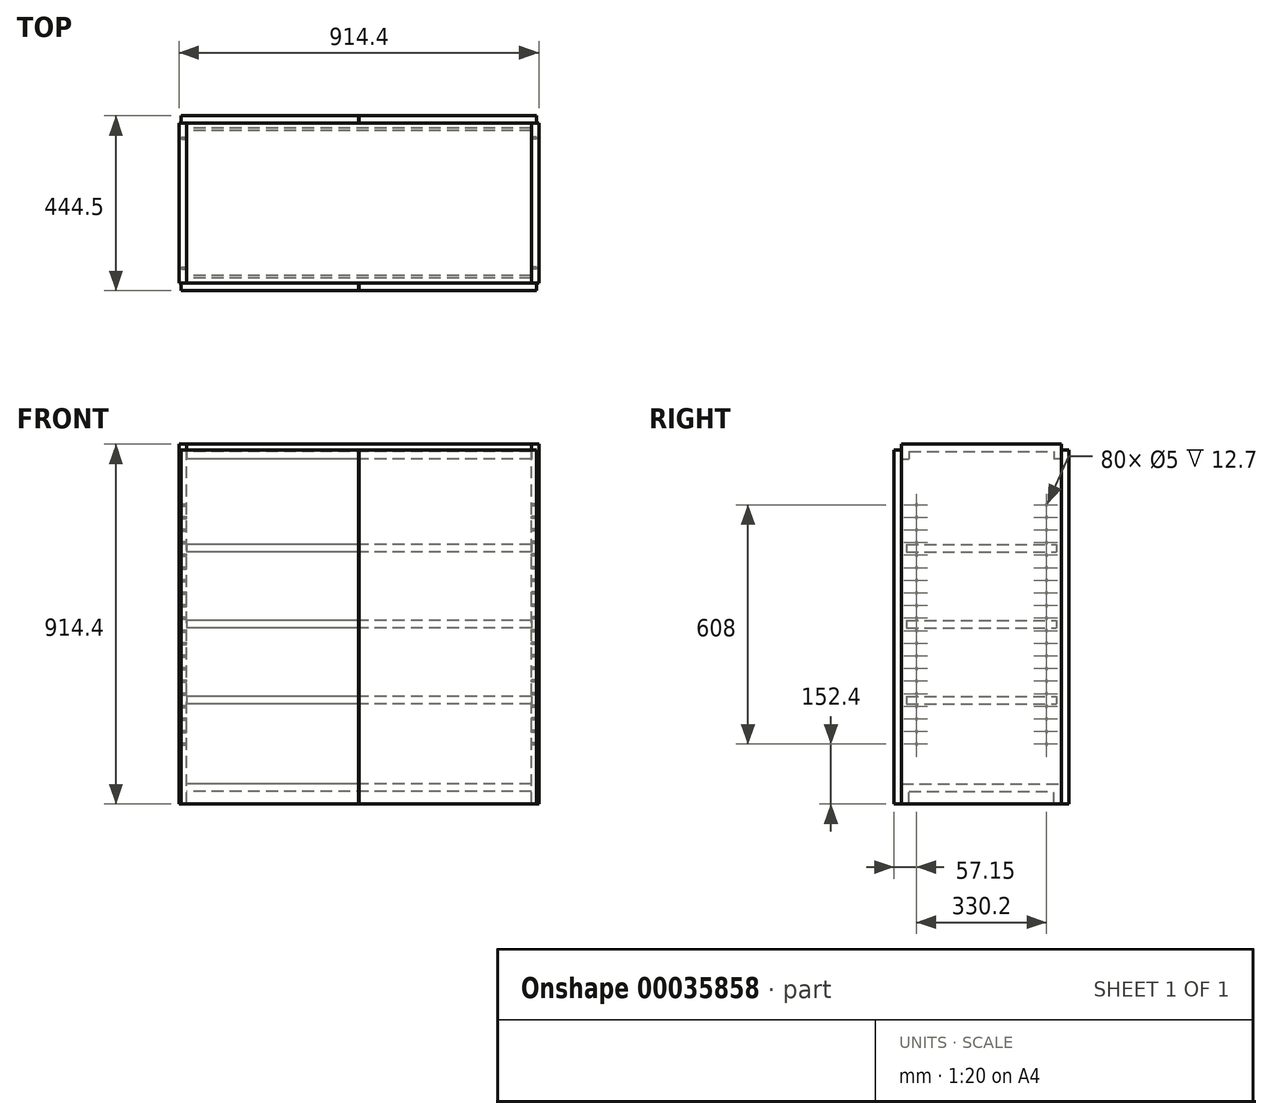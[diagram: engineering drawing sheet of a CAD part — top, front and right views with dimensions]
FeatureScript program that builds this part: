
annotation { "Feature Type Name" : "Feature", "Feature Type Description" : "" }
export const myFeature = defineFeature(function(context is Context, id is Id, definition is map)
    precondition{}
    {
        {
            var Q0;
            Q0=qCreatedBy(makeId("Right.planeOp"),FACE);
            var sketch = newSketch(context, id + "F0", { "sketchPlane" : qUnion([Q0])});
            skLineSegment(sketch, "E0.bottom", {"start": v(0, 0) * mm, "end": v(406.4, 0) * mm});
            skLineSegment(sketch, "E0.top", {"start": v(0, 914.4) * mm, "end": v(406.4, 914.4) * mm});
            skLineSegment(sketch, "E0.left", {"start": v(0, 0) * mm, "end": v(0, 914.4) * mm});
            skLineSegment(sketch, "E0.right", {"start": v(406.4, 0) * mm, "end": v(406.4, 914.4) * mm});
            skSolve(sketch);
        }
        {
            var Q0;
            Q0 = qSketchRegion(id + "F0", true);
            extrude(context, id + "F1", {"entities" : qUnion([Q0]), "depth" : 19.05 * mm});
        }
        {
            var Q0;
            Q0=makeQuery(id+"F1.opExtrude","CAP_FACE",FACE,{"disambiguationData":[OSD([sQuery(id+"F0.wireOp",EDGE,"E0.bottom"),sQuery(id+"F0.wireOp",EDGE,"E0.top"),sQuery(id+"F0.wireOp",EDGE,"E0.left"),sQuery(id+"F0.wireOp",EDGE,"E0.right")])],"isStart":false});
            var sketch = newSketch(context, id + "F2", { "sketchPlane" : qUnion([Q0])});
            skCircle(sketch, "E1", {"center": v(38.1, 152.4) * mm, "radius": 2.5 * mm});
            skCircle(sketch, "E2.0.1.0", {"center": v(38.1, 184.4) * mm, "radius": 2.5 * mm});
            skCircle(sketch, "E2.0.2.0", {"center": v(38.1, 216.4) * mm, "radius": 2.5 * mm});
            skCircle(sketch, "E2.0.3.0", {"center": v(38.1, 248.4) * mm, "radius": 2.5 * mm});
            skCircle(sketch, "E2.0.4.0", {"center": v(38.1, 280.4) * mm, "radius": 2.5 * mm});
            skCircle(sketch, "E2.0.5.0", {"center": v(38.1, 312.4) * mm, "radius": 2.5 * mm});
            skCircle(sketch, "E2.0.6.0", {"center": v(38.1, 344.4) * mm, "radius": 2.5 * mm});
            skCircle(sketch, "E2.0.7.0", {"center": v(38.1, 376.4) * mm, "radius": 2.5 * mm});
            skCircle(sketch, "E2.0.8.0", {"center": v(38.1, 408.4) * mm, "radius": 2.5 * mm});
            skCircle(sketch, "E2.0.9.0", {"center": v(38.1, 440.4) * mm, "radius": 2.5 * mm});
            skCircle(sketch, "E2.0.10.0", {"center": v(38.1, 472.4) * mm, "radius": 2.5 * mm});
            skCircle(sketch, "E2.0.11.0", {"center": v(38.1, 504.4) * mm, "radius": 2.5 * mm});
            skCircle(sketch, "E2.0.12.0", {"center": v(38.1, 536.4) * mm, "radius": 2.5 * mm});
            skCircle(sketch, "E2.0.13.0", {"center": v(38.1, 568.4) * mm, "radius": 2.5 * mm});
            skCircle(sketch, "E2.0.14.0", {"center": v(38.1, 600.4) * mm, "radius": 2.5 * mm});
            skCircle(sketch, "E2.0.15.0", {"center": v(38.1, 632.4) * mm, "radius": 2.5 * mm});
            skCircle(sketch, "E2.0.16.0", {"center": v(38.1, 664.4) * mm, "radius": 2.5 * mm});
            skCircle(sketch, "E2.0.17.0", {"center": v(38.1, 696.4) * mm, "radius": 2.5 * mm});
            skCircle(sketch, "E2.0.18.0", {"center": v(38.1, 728.4) * mm, "radius": 2.5 * mm});
            skCircle(sketch, "E2.0.19.0", {"center": v(38.1, 760.4) * mm, "radius": 2.5 * mm});
            skCircle(sketch, "E2.1.0.0", {"center": v(368.3, 152.4) * mm, "radius": 2.5 * mm});
            skCircle(sketch, "E2.1.1.0", {"center": v(368.3, 184.4) * mm, "radius": 2.5 * mm});
            skCircle(sketch, "E2.1.2.0", {"center": v(368.3, 216.4) * mm, "radius": 2.5 * mm});
            skCircle(sketch, "E2.1.3.0", {"center": v(368.3, 248.4) * mm, "radius": 2.5 * mm});
            skCircle(sketch, "E2.1.4.0", {"center": v(368.3, 280.4) * mm, "radius": 2.5 * mm});
            skCircle(sketch, "E2.1.5.0", {"center": v(368.3, 312.4) * mm, "radius": 2.5 * mm});
            skCircle(sketch, "E2.1.6.0", {"center": v(368.3, 344.4) * mm, "radius": 2.5 * mm});
            skCircle(sketch, "E2.1.7.0", {"center": v(368.3, 376.4) * mm, "radius": 2.5 * mm});
            skCircle(sketch, "E2.1.8.0", {"center": v(368.3, 408.4) * mm, "radius": 2.5 * mm});
            skCircle(sketch, "E2.1.9.0", {"center": v(368.3, 440.4) * mm, "radius": 2.5 * mm});
            skCircle(sketch, "E2.1.10.0", {"center": v(368.3, 472.4) * mm, "radius": 2.5 * mm});
            skCircle(sketch, "E2.1.11.0", {"center": v(368.3, 504.4) * mm, "radius": 2.5 * mm});
            skCircle(sketch, "E2.1.12.0", {"center": v(368.3, 536.4) * mm, "radius": 2.5 * mm});
            skCircle(sketch, "E2.1.13.0", {"center": v(368.3, 568.4) * mm, "radius": 2.5 * mm});
            skCircle(sketch, "E2.1.14.0", {"center": v(368.3, 600.4) * mm, "radius": 2.5 * mm});
            skCircle(sketch, "E2.1.15.0", {"center": v(368.3, 632.4) * mm, "radius": 2.5 * mm});
            skCircle(sketch, "E2.1.16.0", {"center": v(368.3, 664.4) * mm, "radius": 2.5 * mm});
            skCircle(sketch, "E2.1.17.0", {"center": v(368.3, 696.4) * mm, "radius": 2.5 * mm});
            skCircle(sketch, "E2.1.18.0", {"center": v(368.3, 728.4) * mm, "radius": 2.5 * mm});
            skCircle(sketch, "E2.1.19.0", {"center": v(368.3, 760.4) * mm, "radius": 2.5 * mm});
            skLineSegment(sketch, "E2.direction1", {"start": v(38.1, 152.4) * mm, "end": v(368.3, 152.4) * mm, "construction": true});
            skLineSegment(sketch, "E2.direction2", {"start": v(38.1, 152.4) * mm, "end": v(38.1, 184.4) * mm, "construction": true});
            skSolve(sketch);
        }
        {
            var Q0;
            Q0 = qSketchRegion(id + "F2", true);
            extrude(context, id + "F3", {"entities" : qUnion([Q0]), "operationType" : NewBodyOperationType.REMOVE, "oppositeDirection" : true, "depth" : 12.7 * mm});
        }
        {
            var Q0;
            Q0=makeQuery(id+"F1.opExtrude","CAP_FACE",FACE,{"disambiguationData":[OSD([sQuery(id+"F0.wireOp",EDGE,"E0.bottom"),sQuery(id+"F0.wireOp",EDGE,"E0.top"),sQuery(id+"F0.wireOp",EDGE,"E0.left"),sQuery(id+"F0.wireOp",EDGE,"E0.right")])],"isStart":false});
            var sketch = newSketch(context, id + "F4", { "sketchPlane" : qUnion([Q0])});
            skLineSegment(sketch, "E3.bottom", {"start": v(0, 914.4) * mm, "end": v(19.05, 914.4) * mm});
            skLineSegment(sketch, "E3.top", {"start": v(0, 876.3) * mm, "end": v(19.05, 876.3) * mm});
            skLineSegment(sketch, "E3.left", {"start": v(0, 914.4) * mm, "end": v(0, 876.3) * mm});
            skLineSegment(sketch, "E3.right", {"start": v(19.05, 914.4) * mm, "end": v(19.05, 876.3) * mm});
            skLineSegment(sketch, "E4.bottom", {"start": v(406.4, 914.4) * mm, "end": v(387.35, 914.4) * mm});
            skLineSegment(sketch, "E4.top", {"start": v(406.4, 876.3) * mm, "end": v(387.35, 876.3) * mm});
            skLineSegment(sketch, "E4.left", {"start": v(406.4, 914.4) * mm, "end": v(406.4, 876.3) * mm});
            skLineSegment(sketch, "E4.right", {"start": v(387.35, 914.4) * mm, "end": v(387.35, 876.3) * mm});
            skLineSegment(sketch, "E5.bottom", {"start": v(19.05, 914.4) * mm, "end": v(387.35, 914.4) * mm});
            skLineSegment(sketch, "E5.top", {"start": v(19.05, 895.35) * mm, "end": v(387.35, 895.35) * mm});
            skLineSegment(sketch, "E5.left", {"start": v(19.05, 914.4) * mm, "end": v(19.05, 895.35) * mm});
            skLineSegment(sketch, "E5.right", {"start": v(387.35, 914.4) * mm, "end": v(387.35, 895.35) * mm});
            skLineSegment(sketch, "E6.bottom", {"start": v(0, 0) * mm, "end": v(19.05, 0) * mm});
            skLineSegment(sketch, "E6.top", {"start": v(0, 50.8) * mm, "end": v(19.05, 50.8) * mm});
            skLineSegment(sketch, "E6.left", {"start": v(0, 0) * mm, "end": v(0, 50.8) * mm});
            skLineSegment(sketch, "E6.right", {"start": v(19.05, 0) * mm, "end": v(19.05, 50.8) * mm});
            skLineSegment(sketch, "E7.bottom", {"start": v(406.4, 0) * mm, "end": v(387.35, 0) * mm});
            skLineSegment(sketch, "E7.top", {"start": v(406.4, 50.8) * mm, "end": v(387.35, 50.8) * mm});
            skLineSegment(sketch, "E7.left", {"start": v(406.4, 0) * mm, "end": v(406.4, 50.8) * mm});
            skLineSegment(sketch, "E7.right", {"start": v(387.35, 0) * mm, "end": v(387.35, 50.8) * mm});
            skLineSegment(sketch, "E8.bottom", {"start": v(19.05, 50.8) * mm, "end": v(387.35, 50.8) * mm});
            skLineSegment(sketch, "E8.top", {"start": v(19.05, 32.58) * mm, "end": v(387.35, 32.58) * mm});
            skLineSegment(sketch, "E8.left", {"start": v(19.05, 50.8) * mm, "end": v(19.05, 32.58) * mm});
            skLineSegment(sketch, "E8.right", {"start": v(387.35, 50.8) * mm, "end": v(387.35, 32.58) * mm});
            skLineSegment(sketch, "E9.bottom", {"start": v(12.7, 273.28) * mm, "end": v(393.7, 273.28) * mm});
            skLineSegment(sketch, "E9.top", {"start": v(12.7, 254.23) * mm, "end": v(393.7, 254.23) * mm});
            skLineSegment(sketch, "E9.left", {"start": v(12.7, 273.28) * mm, "end": v(12.7, 254.23) * mm});
            skLineSegment(sketch, "E9.right", {"start": v(393.7, 273.28) * mm, "end": v(393.7, 254.23) * mm});
            skLineSegment(sketch, "E10.0.1.0", {"start": v(12.7, 447.27) * mm, "end": v(393.7, 447.27) * mm});
            skLineSegment(sketch, "E10.0.1.1", {"start": v(12.7, 466.32) * mm, "end": v(12.7, 447.27) * mm});
            skLineSegment(sketch, "E10.0.1.2", {"start": v(12.7, 466.32) * mm, "end": v(393.7, 466.32) * mm});
            skLineSegment(sketch, "E10.0.1.3", {"start": v(393.7, 466.32) * mm, "end": v(393.7, 447.27) * mm});
            skLineSegment(sketch, "E10.0.2.0", {"start": v(12.7, 640.3) * mm, "end": v(393.7, 640.3) * mm});
            skLineSegment(sketch, "E10.0.2.1", {"start": v(12.7, 659.36) * mm, "end": v(12.7, 640.3) * mm});
            skLineSegment(sketch, "E10.0.2.2", {"start": v(12.7, 659.36) * mm, "end": v(393.7, 659.36) * mm});
            skLineSegment(sketch, "E10.0.2.3", {"start": v(393.7, 659.36) * mm, "end": v(393.7, 640.3) * mm});
            skLineSegment(sketch, "E10.direction1", {"start": v(12.7, 254.23) * mm, "end": v(38.1, 254.23) * mm, "construction": true});
            skLineSegment(sketch, "E10.direction2", {"start": v(12.7, 254.23) * mm, "end": v(12.7, 447.27) * mm, "construction": true});
            skSolve(sketch);
        }
        {
            var Q0;
            Q0=qCreatedBy(makeId("Right.planeOp"),FACE);
            cPlane(context, id + "F5", {"entities" : qUnion([Q0]), "cplaneType" : CPlaneType.OFFSET, "offset" : 457.2 * mm, "width" : 152.4 * mm, "height" : 152.4 * mm});
        }
        {
            var Q0;
            {var subQ0=sQuery(id+"F4.wireOp",EDGE,"E8.bottom");var subQ10=sQuery(id+"F4.wireOp",EDGE,"E7.bottom");var subQ12=sQuery(id+"F4.wireOp",EDGE,"E6.bottom");var subQ13=sQuery(id+"F4.wireOp",EDGE,"E5.bottom");var subQ15=sQuery(id+"F4.wireOp",EDGE,"E3.bottom");var subQ20=sQuery(id+"F4.wireOp",EDGE,"E4.bottom");Q0=qUnion([makeQuery(id+"F4.imprint","IMPRINT",FACE,{"disambiguationData":[TD([[makeQuery(id+"F4.imprint","IMPRINT",EDGE,{"derivedFrom":sQuery(id+"F4.wireOp",EDGE,"E9.bottom")}),-1.0]])]}),makeQuery(id+"F4.imprint","IMPRINT",FACE,{"disambiguationData":[TD([[makeQuery(id+"F4.imprint","IMPRINT",EDGE,{"derivedFrom":sQuery(id+"F4.wireOp",EDGE,"E10.0.1.0")}),1.0]])]}),makeQuery(id+"F4.imprint","IMPRINT",FACE,{"disambiguationData":[TD([[makeQuery(id+"F4.imprint","IMPRINT",EDGE,{"derivedFrom":sQuery(id+"F4.wireOp",EDGE,"E10.0.2.0")}),1.0]])]}),makeQuery(id+"F4.imprint","IMPRINT",FACE,{"disambiguationData":[TD([[makeQuery(id+"F4.imprint","IMPRINT",EDGE,{"derivedFrom":subQ15}),-1.0]])]}),makeQuery(id+"F4.imprint","IMPRINT",FACE,{"disambiguationData":[TD([[makeQuery(id+"F4.imprint","IMPRINT",EDGE,{"derivedFrom":subQ20}),-1.0]])]}),makeQuery(id+"F4.imprint","IMPRINT",FACE,{"disambiguationData":[TD([[makeQuery(id+"F4.imprint","IMPRINT",EDGE,{"derivedFrom":subQ13}),-1.0]])]}),makeQuery(id+"F4.imprint","IMPRINT",FACE,{"disambiguationData":[TD([[makeQuery(id+"F4.imprint","IMPRINT",EDGE,{"derivedFrom":subQ12}),1.0]])]}),makeQuery(id+"F4.imprint","IMPRINT",FACE,{"disambiguationData":[TD([[makeQuery(id+"F4.imprint","IMPRINT",EDGE,{"derivedFrom":subQ10}),1.0]])]}),makeQuery(id+"F4.imprint","IMPRINT",FACE,{"disambiguationData":[TD([[makeQuery(id+"F4.imprint","IMPRINT",EDGE,{"derivedFrom":subQ0}),-1.0]])]})]);}
            extrude(context, id + "F6", {"entities" : qUnion([Q0]), "depth" : 876.3 * mm});
        }
        {
            var Q0;
            Q0=makeQuery(id+"F1.opExtrude","SWEPT_BODY",BODY,{"disambiguationData":[OSD([sQuery(id+"F0.wireOp",EDGE,"E0.bottom"),sQuery(id+"F0.wireOp",EDGE,"E0.top"),sQuery(id+"F0.wireOp",EDGE,"E0.left"),sQuery(id+"F0.wireOp",EDGE,"E0.right")])]});
            var Q1;
            Q1=qCreatedBy(id+"F5.planeOp",FACE);
            mirror(context, id + "F7", {"entities" : qUnion([Q0]), "mirrorPlane" : qUnion([Q1])});
        }
        {
            var Q0;
            Q0=makeQuery(id+"F6.opExtrude","SWEPT_FACE",FACE,{"disambiguationData":[OSD([sQuery(id+"F4.wireOp",EDGE,"E3.left")])]});
            var sketch = newSketch(context, id + "F8", { "sketchPlane" : qUnion([Q0])});
            skLineSegment(sketch, "E11.bottom", {"start": v(6.04, 899.84) * mm, "end": v(456.9, 899.84) * mm});
            skLineSegment(sketch, "E11.top", {"start": v(6.04, 0) * mm, "end": v(456.9, 0) * mm});
            skLineSegment(sketch, "E11.left", {"start": v(6.04, 899.84) * mm, "end": v(6.04, 0) * mm});
            skLineSegment(sketch, "E11.right", {"start": v(456.9, 899.84) * mm, "end": v(456.9, 0) * mm});
            skSolve(sketch);
        }
        {
            var Q0;
            Q0 = qSketchRegion(id + "F8", true);
            extrude(context, id + "F9", {"entities" : qUnion([Q0]), "depth" : 19.05 * mm});
        }
        {
            var Q0;
            Q0=makeQuery(id+"F9.opExtrude","SWEPT_BODY",BODY,{"disambiguationData":[OSD([sQuery(id+"F8.wireOp",EDGE,"E11.bottom"),sQuery(id+"F8.wireOp",EDGE,"E11.top"),sQuery(id+"F8.wireOp",EDGE,"E11.left"),sQuery(id+"F8.wireOp",EDGE,"E11.right")])]});
            var Q1;
            Q1=qCreatedBy(id+"F5.planeOp",FACE);
            mirror(context, id + "F10", {"entities" : qUnion([Q0]), "mirrorPlane" : qUnion([Q1])});
        }
        {
            var Q0;
            Q0=qCreatedBy(makeId("Front.planeOp"),FACE);
            cPlane(context, id + "F11", {"entities" : qUnion([Q0]), "cplaneType" : CPlaneType.OFFSET, "offset" : 203.2 * mm, "oppositeDirection" : true, "width" : 152.4 * mm, "height" : 152.4 * mm});
        }
        {
            var Q0;
            Q0=makeQuery(id+"F9.opExtrude","SWEPT_BODY",BODY,{"disambiguationData":[OSD([sQuery(id+"F8.wireOp",EDGE,"E11.bottom"),sQuery(id+"F8.wireOp",EDGE,"E11.top"),sQuery(id+"F8.wireOp",EDGE,"E11.left"),sQuery(id+"F8.wireOp",EDGE,"E11.right")])]});
            var Q1;
            Q1=makeQuery(id+"F10.opPattern","COPY",BODY,{"derivedFrom":makeQuery(id+"F9.opExtrude","SWEPT_BODY",BODY,{"disambiguationData":[OSD([sQuery(id+"F8.wireOp",EDGE,"E11.bottom"),sQuery(id+"F8.wireOp",EDGE,"E11.top"),sQuery(id+"F8.wireOp",EDGE,"E11.left"),sQuery(id+"F8.wireOp",EDGE,"E11.right")])]}),"instanceName":"1"});
            var Q2;
            Q2=qCreatedBy(id+"F11.planeOp",FACE);
            mirror(context, id + "F12", {"entities" : qUnion([Q0, Q1]), "mirrorPlane" : qUnion([Q2])});
        }
    });
